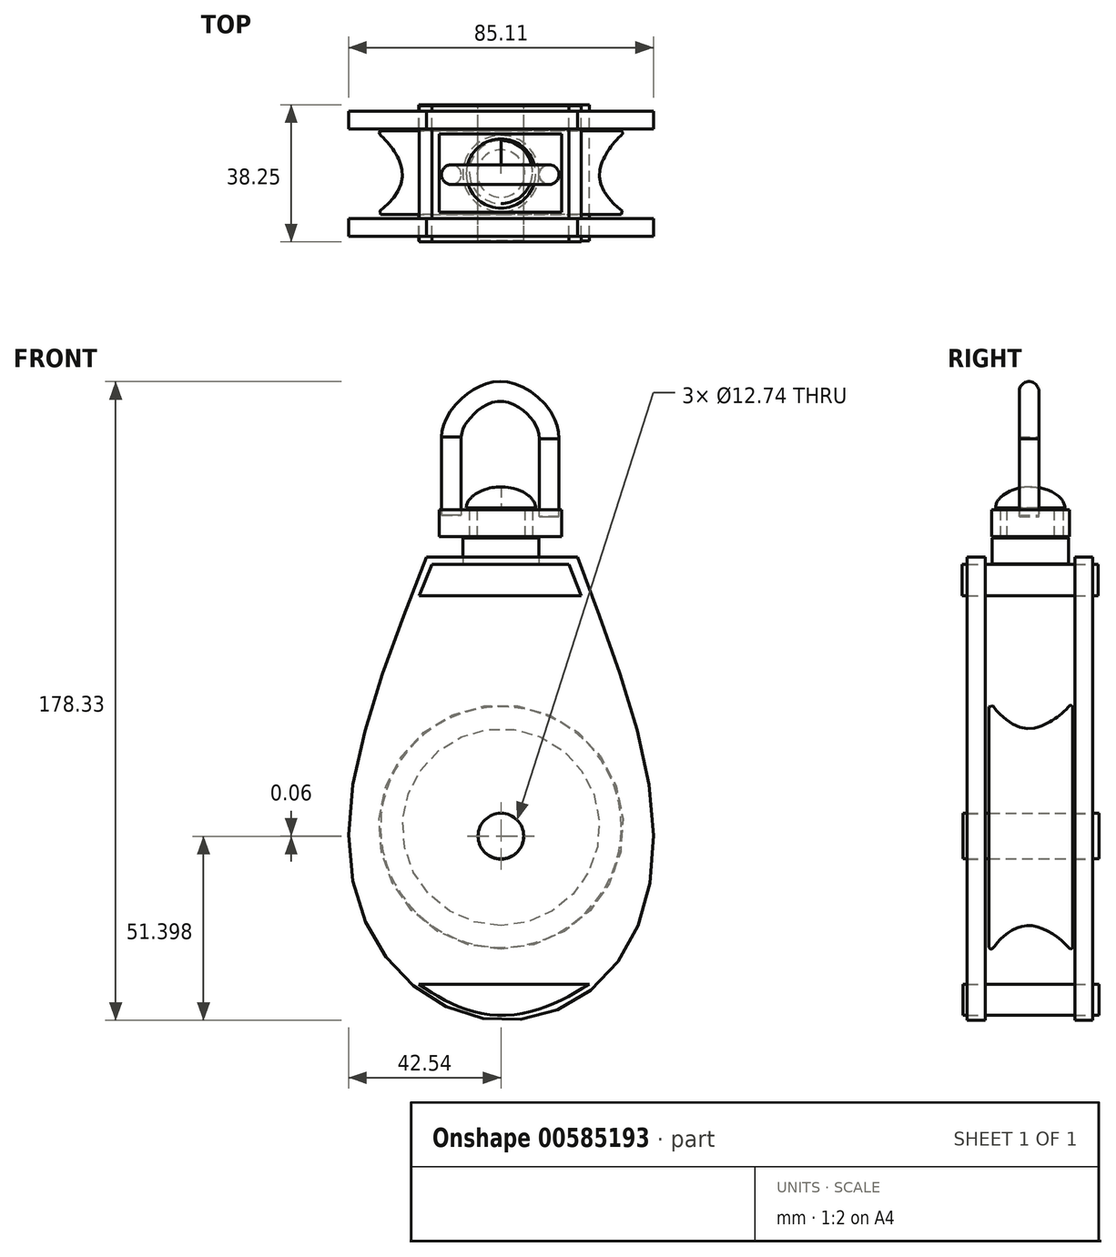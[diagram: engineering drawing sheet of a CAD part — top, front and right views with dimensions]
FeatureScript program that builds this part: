
annotation { "Feature Type Name" : "Feature", "Feature Type Description" : "" }
export const myFeature = defineFeature(function(context is Context, id is Id, definition is map)
    precondition{}
    {
        {
            var Q0;
            Q0=qCreatedBy(makeId("Front.planeOp"),FACE);
            var sketch = newSketch(context, id + "F0", { "sketchPlane" : qUnion([Q0])});
            skFitSpline(sketch, "E0", {"points": [v(-20.72, 75.34) * mm, v(-42.5, 0) * mm, v(-29.74, -39.25) * mm, v(0, -53.96) * mm, v(29.87, -41.06) * mm, v(42.5, 0) * mm, v(21.33, 75.34) * mm], "startDerivative": vector(-149.52, -377.23) * mm, "endDerivative": vector(-144.46, 377.95) * mm});
            skLineSegment(sketch, "E1", {"start": v(-20.72, 75.34) * mm, "end": v(21.33, 75.34) * mm});
            skCircle(sketch, "E2", {"center": v(0, -2.58) * mm, "radius": 6.37 * mm});
            skSolve(sketch);
        }
        {
            var Q0;
            Q0=qCreatedBy(makeId("Front.planeOp"),FACE);
            var sketch = newSketch(context, id + "F1", { "sketchPlane" : qUnion([Q0])});
            skLineSegment(sketch, "E3", {"start": v(-22.92, -43.96) * mm, "end": v(24.65, -43.96) * mm});
            skFitSpline(sketch, "E4", {"points": [v(-22.92, -43.96) * mm, v(-12.94, -49.63) * mm, v(-0.4, -52.55) * mm, v(12.99, -50.02) * mm, v(24.65, -43.96) * mm], "startDerivative": vector(40.26, -25.94) * mm, "endDerivative": vector(44.43, 26.33) * mm});
            skLineSegment(sketch, "E5", {"start": v(-19.3, 73.28) * mm, "end": v(18.98, 73.28) * mm});
            skLineSegment(sketch, "E6", {"start": v(18.98, 73.28) * mm, "end": v(22.44, 64.61) * mm});
            skLineSegment(sketch, "E7", {"start": v(22.44, 64.61) * mm, "end": v(-22.75, 64.61) * mm});
            skLineSegment(sketch, "E8", {"start": v(-22.75, 64.61) * mm, "end": v(-19.3, 73.28) * mm});
            skSolve(sketch);
        }
        {
            var Q0;
            Q0=qCreatedBy(makeId("Front.planeOp"),FACE);
            var sketch = newSketch(context, id + "F2", { "sketchPlane" : qUnion([Q0])});
            skCircle(sketch, "E9", {"center": v(0, -2.52) * mm, "radius": 6.37 * mm});
            skSolve(sketch);
        }
        {
            var Q0;
            Q0 = qSketchRegion(id + "F0", true);
            extrude(context, id + "F3", {"entities" : qUnion([Q0]), "depth" : 5 * mm, "offsetDistance" : 25 * mm});
        }
        {
            var Q0;
            Q0=makeQuery(id+"F3.opExtrude","SWEPT_BODY",BODY,{"disambiguationData":[OSD([sQuery(id+"F0.wireOp",EDGE,"E0"),sQuery(id+"F0.wireOp",EDGE,"E1"),sQuery(id+"F0.wireOp",EDGE,"E2")])]});
            transform(context, id + "F4", {"entities" : qUnion([Q0]), "transformType" : TransformType.COPY});
        }
        {
            var Q0;
            Q0=makeQuery(id+"F3.opExtrude","SWEPT_BODY",BODY,{"disambiguationData":[OSD([sQuery(id+"F0.wireOp",EDGE,"E0"),sQuery(id+"F0.wireOp",EDGE,"E1"),sQuery(id+"F0.wireOp",EDGE,"E2")])]});
            transform(context, id + "F5", {"entities" : qUnion([Q0]), "transformType" : TransformType.TRANSLATION_3D, "dx" : 0 * mm, "dy" : -30 * mm, "dz" : 0 * mm, "makeCopy" : false});
        }
        {
            var Q0;
            Q0=makeQuery(id+"F1.imprint","IMPRINT",FACE,{"disambiguationData":[TD([[makeQuery(id+"F1.imprint","IMPRINT",EDGE,{"derivedFrom":sQuery(id+"F1.wireOp",EDGE,"E5")}),-1.0]])]});
            extrude(context, id + "F6", {"entities" : qUnion([Q0]), "depth" : 38 * mm, "offsetDistance" : 25 * mm});
        }
        {
            var Q0;
            Q0=makeQuery(id+"F6.opExtrude","SWEPT_BODY",BODY,{"disambiguationData":[OSD([sQuery(id+"F1.wireOp",EDGE,"E5"),sQuery(id+"F1.wireOp",EDGE,"E6"),sQuery(id+"F1.wireOp",EDGE,"E7"),sQuery(id+"F1.wireOp",EDGE,"E8")])]});
            transform(context, id + "F7", {"entities" : qUnion([Q0]), "transformType" : TransformType.TRANSLATION_3D, "dx" : 0 * mm, "dy" : 1.5 * mm, "dz" : 0 * mm, "makeCopy" : false});
        }
        {
            var Q0;
            Q0=qCreatedBy(makeId("Right.planeOp"),FACE);
            var sketch = newSketch(context, id + "F8", { "sketchPlane" : qUnion([Q0])});
            skLineSegment(sketch, "E10", {"start": v(-28.9, 0) * mm, "end": v(-28.9, 33.6) * mm});
            skFitSpline(sketch, "E11", {"points": [v(-28.9, 33.6) * mm, v(-27.02, 32.75) * mm, v(-17.81, 27.5) * mm, v(-7.28, 33) * mm, v(-5.53, 33.6) * mm], "startDerivative": vector(10.1, 22.25) * mm, "endDerivative": vector(10.33, -19.72) * mm});
            skLineSegment(sketch, "E12", {"start": v(-5.53, 33.6) * mm, "end": v(-5.53, 0) * mm});
            skLineSegment(sketch, "E13", {"start": v(-28.9, 0) * mm, "end": v(-5.53, 0) * mm});
            skSolve(sketch);
        }
        {
            var Q0;
            Q0=makeQuery(id+"F8.imprint","IMPRINT",FACE,{"disambiguationData":[TD([[makeQuery(id+"F8.imprint","IMPRINT",EDGE,{"derivedFrom":sQuery(id+"F8.wireOp",EDGE,"E10")}),-1.0]])]});
            var Q1;
            Q1=sQuery(id+"F8.wireOp",EDGE,"E13");
            revolve(context, id + "F9", {"entities" : qUnion([Q0]), "axis" : qUnion([Q1]), "revolveType" : RevolveType.FULL});
        }
        {
            var Q0;
            Q0=makeQuery(id+"F1.imprint","IMPRINT",FACE,{"disambiguationData":[TD([[makeQuery(id+"F1.imprint","IMPRINT",EDGE,{"derivedFrom":sQuery(id+"F1.wireOp",EDGE,"E3")}),-1.0]])]});
            extrude(context, id + "F10", {"entities" : qUnion([Q0]), "depth" : 38 * mm, "offsetDistance" : 25 * mm});
        }
        {
            var Q0;
            Q0=makeQuery(id+"F10.opExtrude","SWEPT_BODY",BODY,{"disambiguationData":[OSD([sQuery(id+"F1.wireOp",EDGE,"E3"),sQuery(id+"F1.wireOp",EDGE,"E4")])]});
            transform(context, id + "F11", {"entities" : qUnion([Q0]), "transformType" : TransformType.TRANSLATION_3D, "dx" : 0 * mm, "dy" : 1.75 * mm, "dz" : 0 * mm, "makeCopy" : false});
        }
        {
            var Q0;
            Q0=makeQuery(id+"F2.imprint","IMPRINT",FACE,{"disambiguationData":[TD([[makeQuery(id+"F2.imprint","IMPRINT",EDGE,{"derivedFrom":sQuery(id+"F2.wireOp",EDGE,"E9")}),1.0]])]});
            extrude(context, id + "F12", {"entities" : qUnion([Q0]), "depth" : 38 * mm, "offsetDistance" : 25 * mm});
        }
        {
            var Q0;
            Q0=makeQuery(id+"F12.opExtrude","SWEPT_BODY",BODY,{"disambiguationData":[OSD([sQuery(id+"F2.wireOp",EDGE,"E9")])]});
            transform(context, id + "F13", {"entities" : qUnion([Q0]), "transformType" : TransformType.TRANSLATION_3D, "dx" : 0 * mm, "dy" : 1.75 * mm, "dz" : 0 * mm, "makeCopy" : false});
        }
        {
            var Q0;
            Q0=makeQuery(id+"F12.opExtrude","SWEPT_BODY",BODY,{"disambiguationData":[OSD([sQuery(id+"F2.wireOp",EDGE,"E9")])]});
            var Q1;
            Q1=makeQuery(id+"F9.opRevolve","SWEPT_BODY",BODY,{"disambiguationData":[OSD([sQuery(id+"F8.wireOp",EDGE,"E10"),sQuery(id+"F8.wireOp",EDGE,"E11"),sQuery(id+"F8.wireOp",EDGE,"E12"),sQuery(id+"F8.wireOp",EDGE,"E13")])]});
            booleanBodies(context, id + "F14", {"operationType" : BooleanOperationType.SUBTRACTION, "tools" : qUnion([Q0]), "targets" : qUnion([Q1]), "keepTools" : true});
        }
        {
            var Q0;
            Q0=qCreatedBy(makeId("Right.planeOp"),FACE);
            var sketch = newSketch(context, id + "F15", { "sketchPlane" : qUnion([Q0])});
            skLineSegment(sketch, "E14", {"start": v(-16.93, 73.39) * mm, "end": v(-16.93, 94.9) * mm});
            skFitSpline(sketch, "E15", {"points": [v(-16.93, 94.9) * mm, v(-7.26, 89.03) * mm], "startDerivative": vector(11.73, 0.65) * mm, "endDerivative": vector(0, -11.08) * mm});
            skLineSegment(sketch, "E16", {"start": v(-7.26, 89.03) * mm, "end": v(-10.3, 89.03) * mm});
            skLineSegment(sketch, "E17", {"start": v(-10.3, 89.03) * mm, "end": v(-10.3, 80.67) * mm});
            skLineSegment(sketch, "E18", {"start": v(-10.3, 80.67) * mm, "end": v(-6.29, 80.67) * mm});
            skLineSegment(sketch, "E19", {"start": v(-6.29, 80.67) * mm, "end": v(-6.29, 73.39) * mm});
            skLineSegment(sketch, "E20", {"start": v(-6.29, 73.39) * mm, "end": v(-16.93, 73.39) * mm});
            skSolve(sketch);
        }
        {
            var Q0;
            Q0=makeQuery(id+"F15.imprint","IMPRINT",FACE,{"disambiguationData":[TD([[makeQuery(id+"F15.imprint","IMPRINT",EDGE,{"derivedFrom":sQuery(id+"F15.wireOp",EDGE,"E14")}),-1.0]])]});
            var Q1;
            Q1=sQuery(id+"F15.wireOp",EDGE,"E14");
            revolve(context, id + "F16", {"entities" : qUnion([Q0]), "axis" : qUnion([Q1]), "revolveType" : RevolveType.FULL});
        }
        {
            var Q0;
            Q0=qCreatedBy(makeId("Front.planeOp"),FACE);
            var sketch = newSketch(context, id + "F17", { "sketchPlane" : qUnion([Q0])});
            skLineSegment(sketch, "E21", {"start": v(10.6, 81.12) * mm, "end": v(-10.55, 81.12) * mm});
            skSolve(sketch);
        }
        {
            var Q0;
            Q0=sQuery(id+"F17.wireOp",EDGE,"E21");
            cPlane(context, id + "F18", {"entities" : qUnion([Q0]), "cplaneType" : CPlaneType.LINE_ANGLE, "offset" : 25 * mm, "angle" : 90 * degree, "width" : 150 * mm, "height" : 150 * mm});
        }
        {
            var Q0;
            Q0=qCreatedBy(id+"F18.planeOp",FACE);
            var sketch = newSketch(context, id + "F19", { "sketchPlane" : qUnion([Q0])});
            skLineSegment(sketch, "E22.bottom", {"start": v(16.96, -28.24) * mm, "end": v(-17.2, -28.24) * mm});
            skLineSegment(sketch, "E22.top", {"start": v(16.96, -6.44) * mm, "end": v(-17.2, -6.44) * mm});
            skLineSegment(sketch, "E22.left", {"start": v(16.96, -28.24) * mm, "end": v(16.96, -6.44) * mm});
            skLineSegment(sketch, "E22.right", {"start": v(-17.2, -28.24) * mm, "end": v(-17.2, -6.44) * mm});
            skCircle(sketch, "E23", {"center": v(0, -17.01) * mm, "radius": 8.8 * mm});
            skSolve(sketch);
        }
        {
            var Q0;
            Q0=makeQuery(id+"F16.opRevolve","SWEPT_BODY",BODY,{"disambiguationData":[OSD([sQuery(id+"F15.wireOp",EDGE,"E14"),sQuery(id+"F15.wireOp",EDGE,"E15"),sQuery(id+"F15.wireOp",EDGE,"E16"),sQuery(id+"F15.wireOp",EDGE,"E17"),sQuery(id+"F15.wireOp",EDGE,"E18"),sQuery(id+"F15.wireOp",EDGE,"E19"),sQuery(id+"F15.wireOp",EDGE,"E20")])]});
            transform(context, id + "F20", {"entities" : qUnion([Q0]), "transformType" : TransformType.TRANSLATION_3D, "dx" : 0 * mm, "dy" : -0.5 * mm, "dz" : 0 * mm, "makeCopy" : false});
        }
        {
            var Q0;
            Q0 = qSketchRegion(id + "F19", true);
            extrude(context, id + "F21", {"entities" : qUnion([Q0]), "depth" : 7.5 * mm, "offsetDistance" : 25 * mm});
        }
        {
            var Q0;
            Q0=qCreatedBy(id+"F18.planeOp",FACE);
            var sketch = newSketch(context, id + "F22", { "sketchPlane" : qUnion([Q0])});
            skLineSegment(sketch, "E24", {"start": v(-12.78, -17.83) * mm, "end": v(13.57, -17.83) * mm});
            skSolve(sketch);
        }
        {
            var Q0;
            Q0=sQuery(id+"F22.wireOp",EDGE,"E24");
            cPlane(context, id + "F23", {"entities" : qUnion([Q0]), "cplaneType" : CPlaneType.LINE_ANGLE, "offset" : 25 * mm, "angle" : 0 * degree, "width" : 150 * mm, "height" : 150 * mm});
        }
        {
            var Q0;
            Q0=makeQuery(id+"F21.opExtrude","CAP_FACE",FACE,{"disambiguationData":[OSD([sQuery(id+"F19.wireOp",EDGE,"E22.bottom"),sQuery(id+"F19.wireOp",EDGE,"E22.top"),sQuery(id+"F19.wireOp",EDGE,"E22.left"),sQuery(id+"F19.wireOp",EDGE,"E22.right"),sQuery(id+"F19.wireOp",EDGE,"E23")])],"isStart":false});
            var sketch = newSketch(context, id + "F24", { "sketchPlane" : qUnion([Q0])});
            skCircle(sketch, "E25", {"center": v(13.45, -17.74) * mm, "radius": 2.75 * mm});
            skSolve(sketch);
        }
        {
            var Q0;
            Q0=qCreatedBy(id+"F23.planeOp",FACE);
            var sketch = newSketch(context, id + "F25", { "sketchPlane" : qUnion([Q0])});
            skLineSegment(sketch, "E26", {"start": v(-13.37, 88.84) * mm, "end": v(-13.37, 110.63) * mm});
            skLineSegment(sketch, "E27", {"start": v(13.77, 110.63) * mm, "end": v(13.77, 88.84) * mm});
            skFitSpline(sketch, "E28", {"points": [v(-13.37, 110.63) * mm, v(-9.01, 119.35) * mm, v(0, 123.51) * mm, v(8.82, 119.75) * mm, v(13.77, 110.63) * mm], "startDerivative": vector(0, 38.94) * mm, "endDerivative": vector(0, -39.9) * mm});
            skSolve(sketch);
        }
        {
            var Q0;
            Q0=makeQuery(id+"F24.imprint","IMPRINT",FACE,{"disambiguationData":[TD([[makeQuery(id+"F24.imprint","IMPRINT",EDGE,{"derivedFrom":sQuery(id+"F24.wireOp",EDGE,"E25")}),1.0]])]});
            var Q1;
            Q1=sQuery(id+"F25.wireOp",EDGE,"E26");
            var Q2;
            Q2=sQuery(id+"F25.wireOp",EDGE,"E28");
            var Q3;
            Q3=sQuery(id+"F25.wireOp",EDGE,"E27");
            sweep(context, id + "F26", {"profiles" : qUnion([Q0]), "path" : qUnion([Q1, Q2, Q3])});
        }
        {
            var Q0;
            Q0=makeQuery(id+"F26.opSweep","SWEPT_BODY",BODY,{"disambiguationData":[OSD([sQuery(id+"F24.wireOp",EDGE,"E25"),sQuery(id+"F25.wireOp",EDGE,"E27")])]});
            transform(context, id + "F27", {"entities" : qUnion([Q0]), "transformType" : TransformType.TRANSLATION_3D, "dx" : 0 * mm, "dy" : 0 * mm, "dz" : -2 * mm, "makeCopy" : false});
        }
    });
